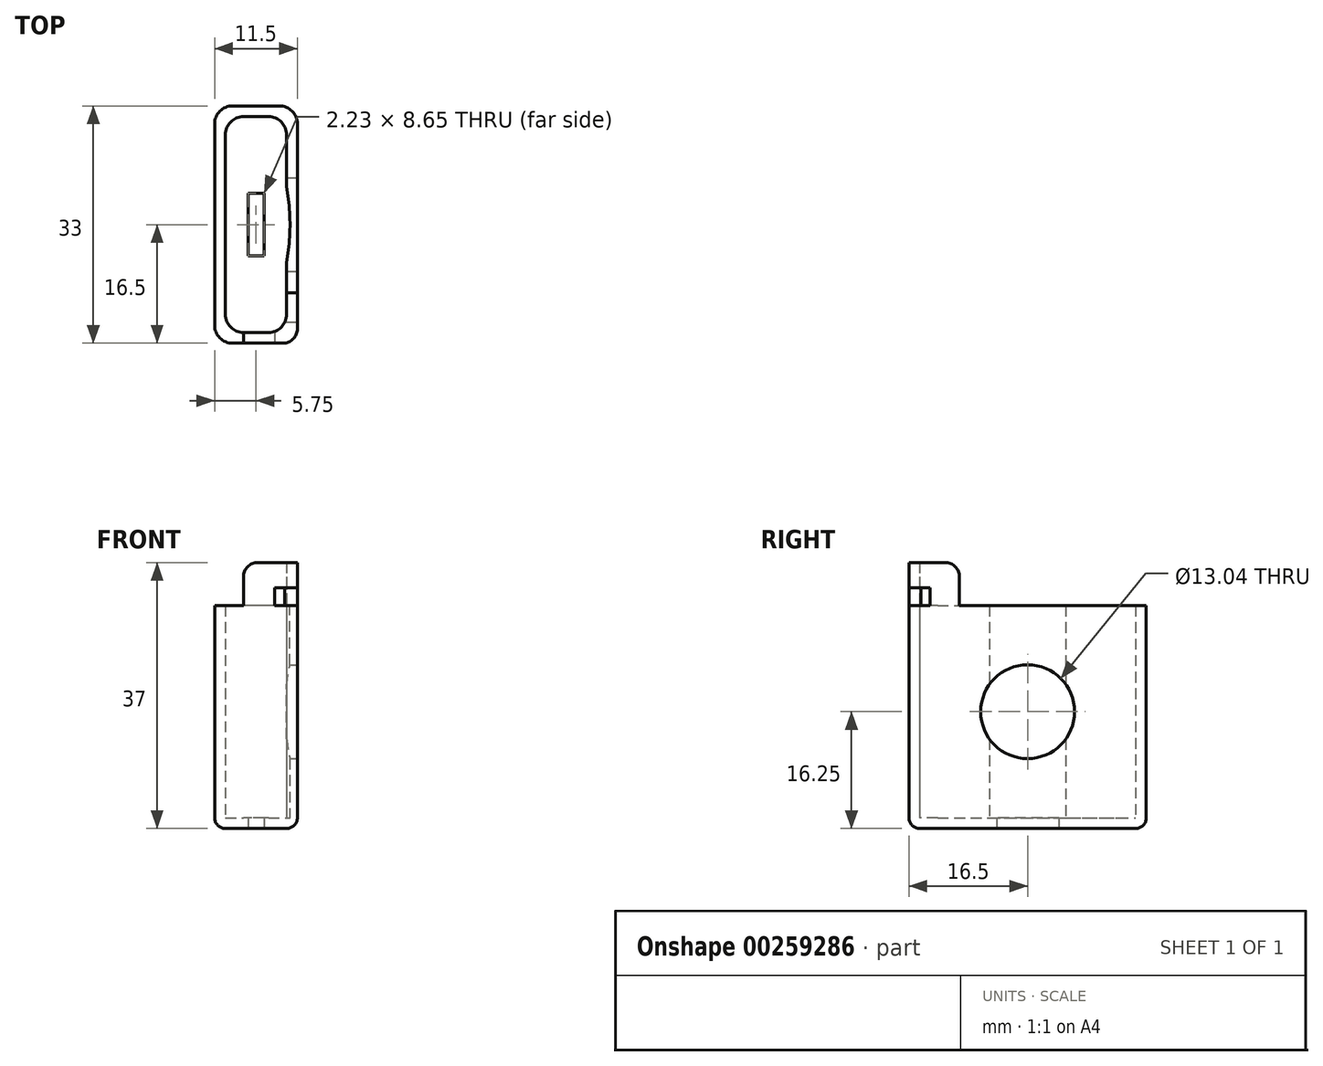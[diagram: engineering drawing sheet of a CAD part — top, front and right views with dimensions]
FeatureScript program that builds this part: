
annotation { "Feature Type Name" : "Feature", "Feature Type Description" : "" }
export const myFeature = defineFeature(function(context is Context, id is Id, definition is map)
    precondition{}
    {
        {
            var Q0;
            Q0=qCreatedBy(makeId("Top.planeOp"),FACE);
            var sketch = newSketch(context, id + "F0", { "sketchPlane" : qUnion([Q0])});
            skLineSegment(sketch, "E0.bottom", {"start": v(1.75, -15) * mm, "end": v(-1.75, -15) * mm});
            skLineSegment(sketch, "E0.top", {"start": v(1.75, 15) * mm, "end": v(-1.75, 15) * mm});
            skLineSegment(sketch, "E0.left", {"start": v(4.25, -12.5) * mm, "end": v(4.25, -5.31) * mm});
            skLineSegment(sketch, "E0.right", {"start": v(-4.25, -12.5) * mm, "end": v(-4.25, 12.5) * mm});
            skPoint(sketch, "E0.middle", {"position": v(0, 0) * mm});
            skLineSegment(sketch, "E1.0", {"start": v(3.25, 16.5) * mm, "end": v(-3.25, 16.5) * mm});
            skLineSegment(sketch, "E1.1", {"start": v(5.75, -16.5) * mm, "end": v(5.75, 14) * mm});
            skLineSegment(sketch, "E1.2", {"start": v(5.75, -16.5) * mm, "end": v(-3.25, -16.5) * mm});
            skLineSegment(sketch, "E1.3", {"start": v(-5.75, -14) * mm, "end": v(-5.75, 14) * mm});
            skPoint(sketch, "E2.visualSharp", {"position": v(-4.25, 15) * mm});
            skArc(sketch, "E2.filletArc", {"start": v(-1.75, 15) * mm, "mid": v(-3.52, 14.27) * mm, "end": v(-4.25, 12.5) * mm});
            skPoint(sketch, "E3.visualSharp", {"position": v(4.25, 15) * mm});
            skArc(sketch, "E3.filletArc", {"start": v(4.25, 12.5) * mm, "mid": v(3.52, 14.27) * mm, "end": v(1.75, 15) * mm});
            skPoint(sketch, "E4.visualSharp", {"position": v(-5.75, 16.5) * mm});
            skArc(sketch, "E4.filletArc", {"start": v(-3.25, 16.5) * mm, "mid": v(-5.02, 15.77) * mm, "end": v(-5.75, 14) * mm});
            skPoint(sketch, "E5.visualSharp", {"position": v(5.75, 16.5) * mm});
            skArc(sketch, "E5.filletArc", {"start": v(5.75, 14) * mm, "mid": v(5.02, 15.77) * mm, "end": v(3.25, 16.5) * mm});
            skPoint(sketch, "E6.visualSharp", {"position": v(-4.25, -15) * mm});
            skArc(sketch, "E6.filletArc", {"start": v(-4.25, -12.5) * mm, "mid": v(-3.52, -14.27) * mm, "end": v(-1.75, -15) * mm});
            skPoint(sketch, "E7.visualSharp", {"position": v(-5.75, -16.5) * mm});
            skArc(sketch, "E7.filletArc", {"start": v(-5.75, -14) * mm, "mid": v(-5.02, -15.77) * mm, "end": v(-3.25, -16.5) * mm});
            skPoint(sketch, "E8.visualSharp", {"position": v(4.25, -15) * mm});
            skArc(sketch, "E8.filletArc", {"start": v(1.75, -15) * mm, "mid": v(3.52, -14.27) * mm, "end": v(4.25, -12.5) * mm});
            skPoint(sketch, "E9.visualSharp", {"position": v(5.75, -16.5) * mm});
            skLineSegment(sketch, "E10.bottom", {"start": v(1.12, 4.33) * mm, "end": v(-1.11, 4.33) * mm});
            skLineSegment(sketch, "E10.top", {"start": v(1.11, -4.32) * mm, "end": v(-1.12, -4.32) * mm});
            skLineSegment(sketch, "E10.left", {"start": v(1.12, 4.33) * mm, "end": v(1.11, -4.32) * mm});
            skLineSegment(sketch, "E10.right", {"start": v(-1.11, 4.33) * mm, "end": v(-1.12, -4.32) * mm});
            skEllipticalArc(sketch, "E11.trimOffspring", {});
            skLineSegment(sketch, "E12.trimOffspring", {"start": v(4.25, 5.31) * mm, "end": v(4.25, 12.5) * mm});
            const initialGuessF0  = {"E11.trimOffspring": [0, 0, 0, 1, 0.012210056185722351, 0.004720231032473186, 4.262233947173465, 5.162544013595915]};
            skSetInitialGuess(sketch, initialGuessF0);
            skSolve(sketch);
        }
        {
            var Q0;
            Q0=makeQuery(id+"F0.imprint","IMPRINT",FACE,{"disambiguationData":[TD([[makeQuery(id+"F0.imprint","IMPRINT",EDGE,{"derivedFrom":sQuery(id+"F0.wireOp",EDGE,"E0.bottom")}),-1.0]])]});
            extrude(context, id + "F1", {"entities" : qUnion([Q0]), "depth" : 1.5 * mm});
        }
        {
            var Q0;
            Q0=makeQuery(id+"F0.imprint","IMPRINT",FACE,{"disambiguationData":[TD([[makeQuery(id+"F0.imprint","IMPRINT",EDGE,{"derivedFrom":sQuery(id+"F0.wireOp",EDGE,"E0.bottom")}),1.0]])]});
            extrude(context, id + "F2", {"entities" : qUnion([Q0]), "operationType" : NewBodyOperationType.ADD, "depth" : 31 * mm});
        }
        {
            var Q0;
            Q0=makeQuery(id+"F2.opExtrude","CAP_FACE",FACE,{"disambiguationData":[OSD([sQuery(id+"F0.wireOp",EDGE,"E0.bottom"),sQuery(id+"F0.wireOp",EDGE,"E0.top"),sQuery(id+"F0.wireOp",EDGE,"E0.left"),sQuery(id+"F0.wireOp",EDGE,"E0.right"),sQuery(id+"F0.wireOp",EDGE,"E1.0"),sQuery(id+"F0.wireOp",EDGE,"E1.1"),sQuery(id+"F0.wireOp",EDGE,"E1.2"),sQuery(id+"F0.wireOp",EDGE,"E1.3"),sQuery(id+"F0.wireOp",EDGE,"E2.filletArc"),sQuery(id+"F0.wireOp",EDGE,"E3.filletArc"),sQuery(id+"F0.wireOp",EDGE,"E4.filletArc"),sQuery(id+"F0.wireOp",EDGE,"E5.filletArc"),sQuery(id+"F0.wireOp",EDGE,"E6.filletArc"),sQuery(id+"F0.wireOp",EDGE,"E7.filletArc"),sQuery(id+"F0.wireOp",EDGE,"E8.filletArc"),sQuery(id+"F0.wireOp",EDGE,"E9.filletArc")])],"isStart":false});
            var sketch = newSketch(context, id + "F3", { "sketchPlane" : qUnion([Q0])});
            skLineSegment(sketch, "E13", {"start": v(-1.75, -16.5) * mm, "end": v(5.75, -16.5) * mm});
            skLineSegment(sketch, "E14", {"start": v(5.75, -16.5) * mm, "end": v(5.75, -9.47) * mm});
            skLineSegment(sketch, "E15", {"start": v(5.75, -9.47) * mm, "end": v(4.25, -9.47) * mm});
            skLineSegment(sketch, "E16", {"start": v(4.25, -9.47) * mm, "end": v(4.25, -12.5) * mm});
            skArc(sketch, "E17", {"start": v(1.75, -15) * mm, "mid": v(3.52, -14.27) * mm, "end": v(4.25, -12.5) * mm});
            skLineSegment(sketch, "E18", {"start": v(1.75, -15) * mm, "end": v(-1.75, -15) * mm});
            skLineSegment(sketch, "E19", {"start": v(4.01, -13.57) * mm, "end": v(5.75, -13.57) * mm});
            skLineSegment(sketch, "E20", {"start": v(2.62, -14.85) * mm, "end": v(2.62, -16.5) * mm});
            skLineSegment(sketch, "E21", {"start": v(-1.75, -15) * mm, "end": v(-1.75, -16.5) * mm});
            skPoint(sketch, "E22.orphan", {"position": v(0, -15) * mm});
            skSolve(sketch);
        }
        {
            var Q0;
            Q0=makeQuery(id+"F2.opExtrude","SWEPT_FACE",FACE,{"disambiguationData":[OSD([sQuery(id+"F0.wireOp",EDGE,"E1.1")])]});
            var sketch = newSketch(context, id + "F4", { "sketchPlane" : qUnion([Q0])});
            skLineSegment(sketch, "E23", {"start": v(0, 0) * mm, "end": v(0, 16.25) * mm});
            skCircle(sketch, "E24", {"center": v(0, 16.25) * mm, "radius": 6.52 * mm});
            skSolve(sketch);
        }
        {
            var Q0;
            Q0=makeQuery(id+"F4.imprint","IMPRINT",FACE,{"disambiguationData":[TD([[makeQuery(id+"F4.imprint","IMPRINT",EDGE,{"derivedFrom":sQuery(id+"F4.wireOp",EDGE,"E24")}),1.0]])]});
            extrude(context, id + "F5", {"entities" : qUnion([Q0]), "operationType" : NewBodyOperationType.REMOVE, "oppositeDirection" : true, "depth" : 2 * mm});
        }
        {
            var Q0;
            Q0=makeQuery(id+"F2.opExtrude","CAP_EDGE",EDGE,{"disambiguationData":[OSD([sQuery(id+"F0.wireOp",EDGE,"E1.1")])],"isStart":true});
            fillet(context, id + "F6", {"entities" : qUnion([Q0]), "radius" : 1.5 * mm, "tangentPropagation" : true, "allowEdgeOverflow" : false});
        }
        {
            var Q0;
            Q0=makeQuery(id+"F3.imprint","IMPRINT",FACE,{"disambiguationData":[TD([[makeQuery(id+"F3.imprint","IMPRINT",EDGE,{"derivedFrom":sQuery(id+"F3.wireOp",EDGE,"q9PxozeP-cDu3-THDV-2qZ5-JNbp6pKrtjRM")}),1.0]])]});
            var Q1;
            Q1=makeQuery(id+"F3.imprint","IMPRINT",FACE,{"disambiguationData":[TD([[makeQuery(id+"F3.imprint","IMPRINT",EDGE,{"derivedFrom":sQuery(id+"F3.wireOp",EDGE,"E14")}),1.0]])]});
            var Q2;
            Q2=makeQuery(id+"F3.imprint","IMPRINT",FACE,{"disambiguationData":[TD([[makeQuery(id+"F3.imprint","IMPRINT",EDGE,{"derivedFrom":sQuery(id+"F3.wireOp",EDGE,"QVA2dT3G-yDjh-z2TK-0i8k-z1P1WwWvy8Ze")}),1.0]])]});
            var Q3;
            Q3=makeQuery(id+"F3.imprint","IMPRINT",FACE,{"disambiguationData":[TD([[makeQuery(id+"F3.imprint","IMPRINT",EDGE,{"derivedFrom":sQuery(id+"F3.wireOp",EDGE,"E18")}),1.0]])]});
            var Q4;
            Q4=makeQuery(id+"F3.imprint","IMPRINT",FACE,{"disambiguationData":[TD([[makeQuery(id+"F3.imprint","IMPRINT",EDGE,{"derivedFrom":sQuery(id+"F3.wireOp",EDGE,"E17")}),-1.0]])]});
            extrude(context, id + "F7", {"entities" : qUnion([Q0, Q1, Q2, Q3, Q4]), "operationType" : NewBodyOperationType.ADD, "depth" : 6 * mm});
        }
        {
            var Q0;
            Q0=makeQuery(id+"F7.opExtrude","CAP_EDGE",EDGE,{"disambiguationData":[OSD([sQuery(id+"F3.wireOp",EDGE,"E21")])],"isStart":false});
            var Q1;
            Q1=makeQuery(id+"F7.opExtrude","CAP_EDGE",EDGE,{"disambiguationData":[OSD([sQuery(id+"F3.wireOp",EDGE,"E15")])],"isStart":false});
            fillet(context, id + "F8", {"entities" : qUnion([Q0, Q1]), "radius" : 2 * mm, "tangentPropagation" : true, "allowEdgeOverflow" : false});
        }
        {
            var Q0;
            {var subQ0=sQuery(id+"F3.wireOp",EDGE,"E19");Q0=makeQuery(id+"F3.imprint","IMPRINT",FACE,{"disambiguationData":[TD([[makeQuery(id+"F3.imprint","IMPRINT",EDGE,{"derivedFrom":subQ0}),-1.0]])]});}
            extrude(context, id + "F9", {"entities" : qUnion([Q0]), "operationType" : NewBodyOperationType.REMOVE, "depth" : 2.5 * mm});
        }
        {
            var Q0;
            {var subQ0=sQuery(id+"F3.wireOp",EDGE,"E17");var subQ1=sQuery(id+"F3.wireOp",EDGE,"E14");var subQ2=sQuery(id+"F3.wireOp",EDGE,"E13");var subQ3=sQuery(id+"F0.wireOp",EDGE,"E1.2");var subQ4=sQuery(id+"F0.wireOp",EDGE,"E1.1");Q0=makeQuery(id+"F9.boolean.opBoolean","SPLIT",EDGE,{"disambiguationData":[TD([makeQuery(id+"F9.opExtrude","CAP_FACE",FACE,{"disambiguationData":[OSD([subQ2,subQ1,subQ0,sQuery(id+"F3.wireOp",EDGE,"E19"),sQuery(id+"F3.wireOp",EDGE,"E20")])],"isStart":false})])],"derivedFrom":makeQuery(id+"F7.boolean.opBoolean","MERGE",EDGE,{"derivedFrom":[makeQuery(id+"F2.opExtrude","SWEPT_EDGE",EDGE,{"disambiguationData":[OSD([subQ4,subQ3])]}),makeQuery(id+"F7.opExtrude","SWEPT_EDGE",EDGE,{"disambiguationData":[OSD([subQ2,subQ1])]})]})});}
            var Q1;
            {var subQ0=sQuery(id+"F0.wireOp",EDGE,"E1.2");var subQ1=sQuery(id+"F0.wireOp",EDGE,"E1.1");var subQ2=sQuery(id+"F3.wireOp",EDGE,"E13");var subQ3=sQuery(id+"F3.wireOp",EDGE,"E14");Q1=makeQuery(id+"F9.boolean.opBoolean","SPLIT",EDGE,{"disambiguationData":[TD([makeQuery(id+"F6.opFillet","BLEND_FACE",FACE,{"disambiguationData":[OSD([subQ1])]})])],"derivedFrom":makeQuery(id+"F7.boolean.opBoolean","MERGE",EDGE,{"derivedFrom":[makeQuery(id+"F2.opExtrude","SWEPT_EDGE",EDGE,{"disambiguationData":[OSD([subQ1,subQ0])]}),makeQuery(id+"F7.opExtrude","SWEPT_EDGE",EDGE,{"disambiguationData":[OSD([subQ2,subQ3])]})]})});}
            fillet(context, id + "F10", {"entities" : qUnion([Q0, Q1]), "radius" : 2 * mm, "tangentPropagation" : true, "allowEdgeOverflow" : false});
        }
    });
